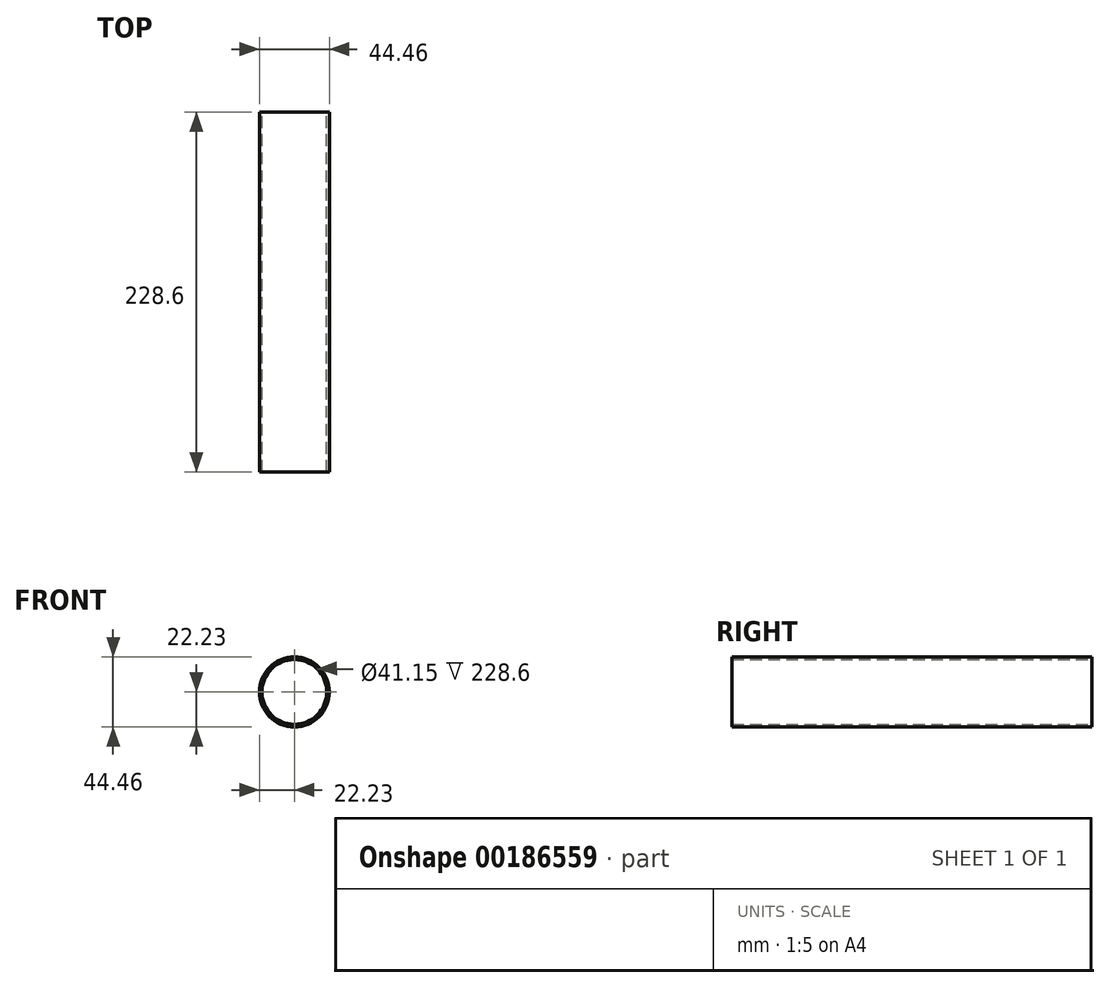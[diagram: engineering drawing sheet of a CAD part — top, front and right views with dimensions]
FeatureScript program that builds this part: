
annotation { "Feature Type Name" : "Feature", "Feature Type Description" : "" }
export const myFeature = defineFeature(function(context is Context, id is Id, definition is map)
    precondition{}
    {
        {
            var Q0;
            Q0=qCreatedBy(makeId("Front.planeOp"),FACE);
            var sketch = newSketch(context, id + "F0", { "sketchPlane" : qUnion([Q0])});
            skCircle(sketch, "E0", {"center": v(0, 0) * mm, "radius": 22.23 * mm});
            skCircle(sketch, "E1", {"center": v(0, 0) * mm, "radius": 20.57 * mm});
            skSolve(sketch);
        }
        {
            var Q0;
            Q0=makeQuery(id+"F0.imprint","IMPRINT",FACE,{"disambiguationData":[TD([[makeQuery(id+"F0.imprint","IMPRINT",EDGE,{"derivedFrom":sQuery(id+"F0.wireOp",EDGE,"E0")}),1.0]])]});
            extrude(context, id + "F1", {"entities" : qUnion([Q0]), "depth" : 228.6 * mm});
        }
    });
